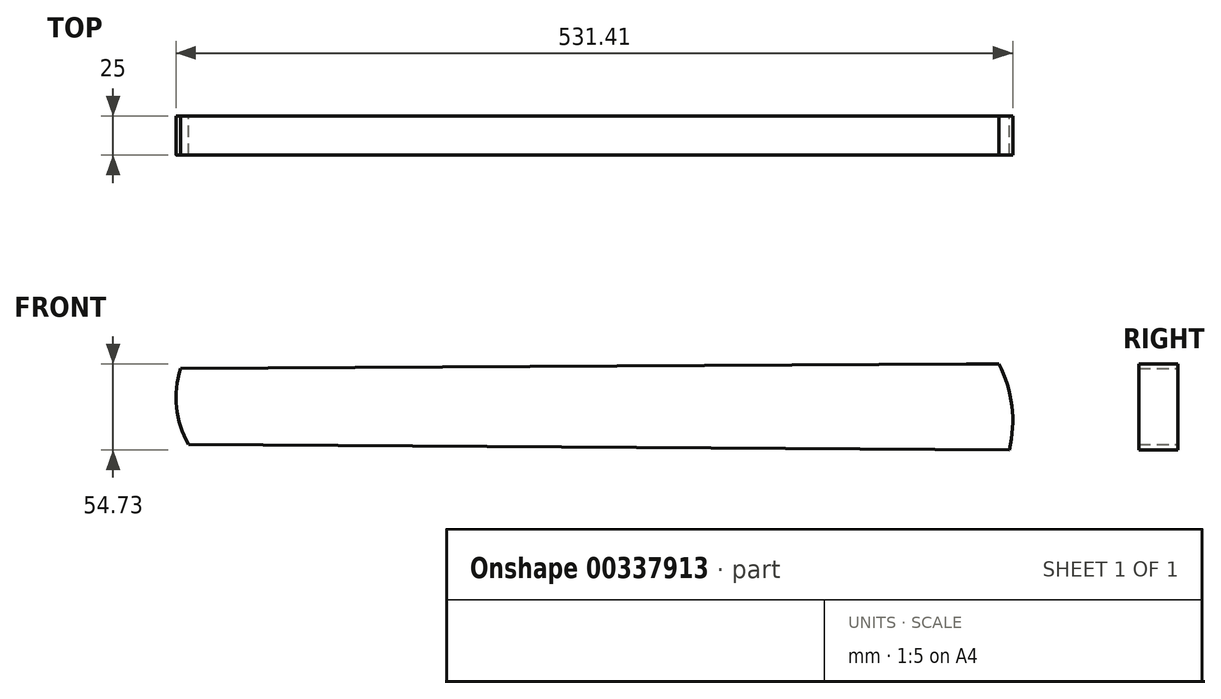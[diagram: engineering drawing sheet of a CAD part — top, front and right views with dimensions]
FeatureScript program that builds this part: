
annotation { "Feature Type Name" : "Feature", "Feature Type Description" : "" }
export const myFeature = defineFeature(function(context is Context, id is Id, definition is map)
    precondition{}
    {
        {
            var Q0;
            Q0=qCreatedBy(makeId("Front.planeOp"),FACE);
            var sketch = newSketch(context, id + "F0", { "sketchPlane" : qUnion([Q0])});
            skLineSegment(sketch, "E0.top", {"start": v(348.78, -158.15) * mm, "end": v(325.9, -158.15) * mm});
            skLineSegment(sketch, "E0.left", {"start": v(348.78, 219.3) * mm, "end": v(348.78, -158.15) * mm});
            skPoint(sketch, "E0.middle", {"position": v(0, 0) * mm});
            skLineSegment(sketch, "E1", {"start": v(-310.5, 344.83) * mm, "end": v(-363.6, 344.83) * mm});
            skFitSpline(sketch, "E2", {"points": [v(-350.67, 344.83) * mm, v(347.35, 254.73) * mm, v(923.32, -91.46) * mm, v(911.37, -154.4) * mm, v(869.65, -185.3) * mm], "startDerivative": vector(1663.46, -7.35) * mm, "endDerivative": vector(-3077.7, -870.32) * mm});
            skLineSegment(sketch, "E3", {"start": v(348.78, 219.3) * mm, "end": v(347.5, 251.23) * mm});
            skLineSegment(sketch, "E4.0", {"start": v(280.23, 190.93) * mm, "end": v(-218.88, 187.87) * mm});
            skPoint(sketch, "E5.newPointA", {"position": v(-350, 535) * mm});
            skLineSegment(sketch, "E6", {"start": v(-318.8, 187.25) * mm, "end": v(-458.7, 455.7) * mm});
            skLineSegment(sketch, "E7", {"start": v(-311.32, 135.27) * mm, "end": v(-457.28, -158.15) * mm});
            skLineSegment(sketch, "E8", {"start": v(-418.69, -158.15) * mm, "end": v(-457.28, -158.15) * mm});
            skArc(sketch, "E9", {"start": v(-218.88, 187.87) * mm, "mid": v(-221.35, 163.28) * mm, "end": v(-213.7, 139.78) * mm});
            skLineSegment(sketch, "E10.trimOffspring", {"start": v(326.04, -158.15) * mm, "end": v(326.04, -159.41) * mm});
            skLineSegment(sketch, "E11", {"start": v(-318.8, 187.25) * mm, "end": v(-310.8, 171.92) * mm});
            skLineSegment(sketch, "E12", {"start": v(-311.32, 135.27) * mm, "end": v(-308.21, 146.05) * mm});
            skArc(sketch, "E13.filletArc", {"start": v(-308.21, 146.05) * mm, "mid": v(-307.02, 159.24) * mm, "end": v(-310.8, 171.92) * mm});
            skLineSegment(sketch, "E14.filletArc", {"start": v(279.23, 184.4) * mm, "end": v(279.23, 184.4) * mm});
            skLineSegment(sketch, "E15", {"start": v(280.23, 190.93) * mm, "end": v(300.92, 190.93) * mm});
            skLineSegment(sketch, "E16.trimOffspring", {"start": v(325.9, -158.15) * mm, "end": v(326.04, -159.41) * mm});
            skLineSegment(sketch, "E17", {"start": v(-287.9, 78.75) * mm, "end": v(-418.69, -158.15) * mm});
            skArc(sketch, "E18.trimOffspring", {"start": v(299.4, 190.93) * mm, "mid": v(299.33, 190.97) * mm, "end": v(299.25, 191) * mm});
            skArc(sketch, "E19.0", {"start": v(307.52, 136.2) * mm, "mid": v(309.15, 164.16) * mm, "end": v(300.92, 190.93) * mm});
            skLineSegment(sketch, "E20", {"start": v(294.6, 136.3) * mm, "end": v(-233.24, 139.91) * mm});
            skArc(sketch, "E21.filletArc", {"start": v(314.46, 116.85) * mm, "mid": v(308.46, 130.58) * mm, "end": v(294.6, 136.3) * mm});
            skLineSegment(sketch, "E22.0", {"start": v(-292.9, 209.2) * mm, "end": v(-421.38, 455.7) * mm});
            skLineSegment(sketch, "E23", {"start": v(-194.49, 188.02) * mm, "end": v(-260.36, 187.61) * mm});
            skArc(sketch, "E24.filletArc", {"start": v(-292.9, 209.2) * mm, "mid": v(-279.92, 193.44) * mm, "end": v(-260.36, 187.61) * mm});
            skLineSegment(sketch, "E25", {"start": v(-457.28, -158.15) * mm, "end": v(348.78, -158.15) * mm, "construction": true});
            skLineSegment(sketch, "E26", {"start": v(-458.7, 455.7) * mm, "end": v(-421.38, 455.7) * mm});
            skLineSegment(sketch, "E27", {"start": v(-297.94, 60.56) * mm, "end": v(-264.12, 121.83) * mm});
            skArc(sketch, "E28.filletArc", {"start": v(-233.24, 139.91) * mm, "mid": v(-251.17, 135.12) * mm, "end": v(-264.12, 121.83) * mm});
            skLineSegment(sketch, "E29", {"start": v(314.46, 116.85) * mm, "end": v(323.78, -158.15) * mm});
            skLineSegment(sketch, "E30", {"start": v(323.78, -158.15) * mm, "end": v(348.78, -158.15) * mm});
            skLineSegment(sketch, "E31", {"start": v(300.92, 190.93) * mm, "end": v(309.64, 190.93) * mm});
            skArc(sketch, "E32.filletArc", {"start": v(309.64, 190.93) * mm, "mid": v(323.78, 196.79) * mm, "end": v(329.64, 210.93) * mm});
            skLineSegment(sketch, "E33", {"start": v(347.5, 251.23) * mm, "end": v(347.5, 286.23) * mm});
            skLineSegment(sketch, "E34", {"start": v(-363.6, 379.83) * mm, "end": v(-381.83, 379.83) * mm});
            skFitSpline(sketch, "E35", {"points": [v(-381.83, 379.83) * mm, v(347.5, 286.23) * mm, v(695.3, 144.82) * mm], "startDerivative": vector(1371.77, -108.32) * mm, "endDerivative": vector(747.87, -376.57) * mm});
            skLineSegment(sketch, "E36", {"start": v(329.64, 210.93) * mm, "end": v(329.64, 260.32) * mm});
            skLineSegment(sketch, "E37", {"start": v(347.5, 286.23) * mm, "end": v(329.64, 260.32) * mm});
            skLineSegment(sketch, "E38", {"start": v(307.52, 136.2) * mm, "end": v(294.6, 136.3) * mm});
            skSolve(sketch);
        }
        {
            var Q0;
            Q0=makeQuery(id+"F0.imprint","IMPRINT",FACE,{"disambiguationData":[TD([[makeQuery(id+"F0.imprint","IMPRINT",EDGE,{"derivedFrom":sQuery(id+"F0.wireOp",EDGE,"E6")}),-1.0]])]});
            var sketch = newSketch(context, id + "F1", { "sketchPlane" : qUnion([Q0])});
            skLineSegment(sketch, "E39.0.0", {"start": v(300.92, 190.93) * mm, "end": v(299.4, 190.93) * mm});
            skLineSegment(sketch, "E39.0.1", {"start": v(299.4, 190.93) * mm, "end": v(280.23, 190.93) * mm});
            skLineSegment(sketch, "E39.0.2", {"start": v(280.23, 190.93) * mm, "end": v(-194.49, 188.02) * mm});
            skLineSegment(sketch, "E39.0.3", {"start": v(-194.49, 188.02) * mm, "end": v(-218.88, 187.87) * mm});
            skArc(sketch, "E39.0.4", {"start": v(-218.88, 187.87) * mm, "mid": v(-221.35, 163.28) * mm, "end": v(-213.7, 139.78) * mm});
            skLineSegment(sketch, "E39.0.5", {"start": v(-213.7, 139.78) * mm, "end": v(294.6, 136.3) * mm});
            skLineSegment(sketch, "E39.0.6", {"start": v(294.6, 136.3) * mm, "end": v(307.52, 136.2) * mm});
            skArc(sketch, "E39.0.7", {"start": v(307.52, 136.2) * mm, "mid": v(309.15, 164.16) * mm, "end": v(300.92, 190.93) * mm});
            skSolve(sketch);
        }
        {
            var Q0;
            Q0 = qSketchRegion(id + "F1", true);
            extrude(context, id + "F2", {"entities" : qUnion([Q0]), "depth" : 25 * mm});
        }
    });
